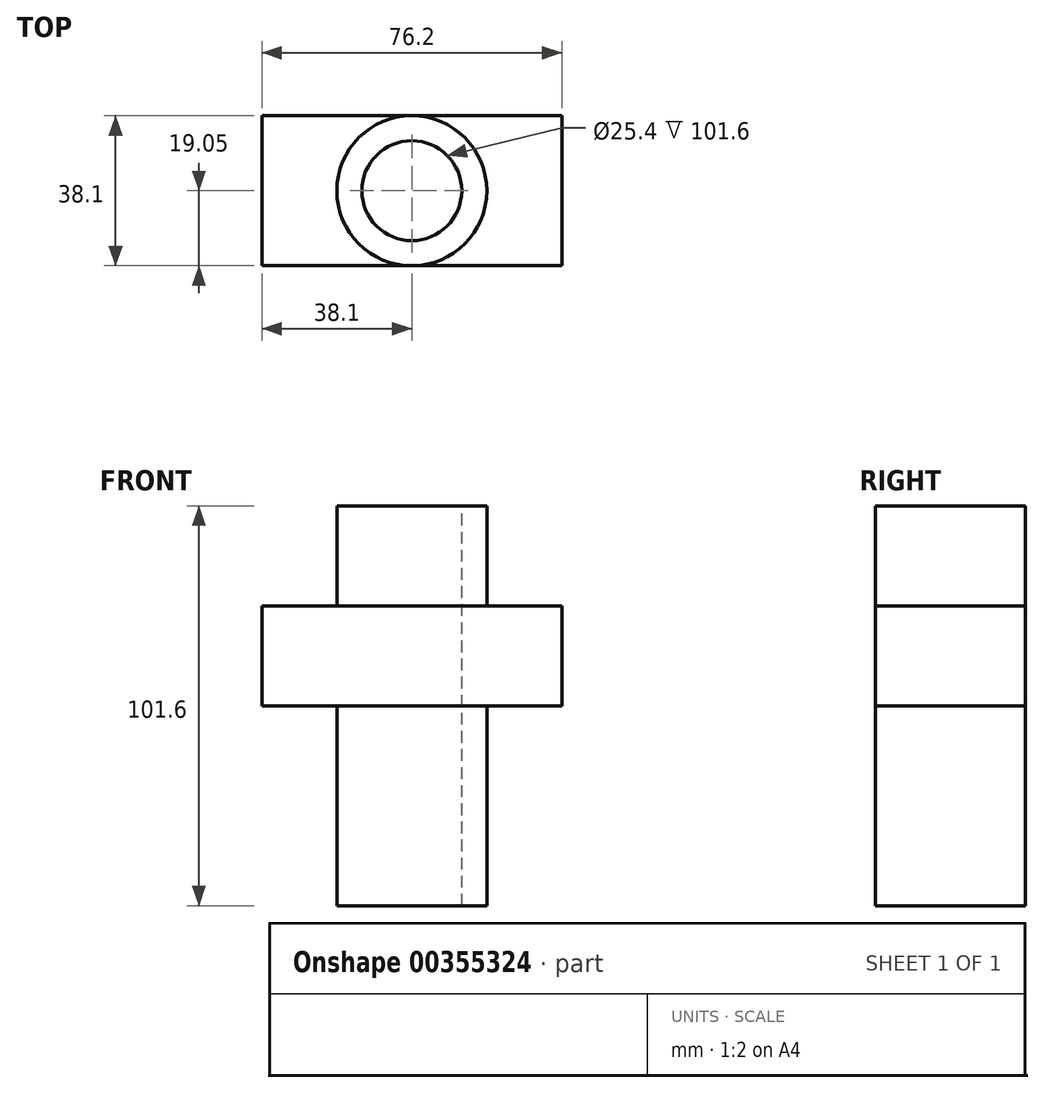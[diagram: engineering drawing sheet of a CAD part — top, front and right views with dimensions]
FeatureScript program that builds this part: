
annotation { "Feature Type Name" : "Feature", "Feature Type Description" : "" }
export const myFeature = defineFeature(function(context is Context, id is Id, definition is map)
    precondition{}
    {
        {
            var Q0;
            Q0=qCreatedBy(makeId("Top.planeOp"),FACE);
            var sketch = newSketch(context, id + "F0", { "sketchPlane" : qUnion([Q0])});
            skLineSegment(sketch, "E0", {"start": v(0, 0) * mm, "end": v(0, 38.1) * mm});
            skLineSegment(sketch, "E1", {"start": v(0, 38.1) * mm, "end": v(76.2, 38.1) * mm});
            skLineSegment(sketch, "E2", {"start": v(76.2, 38.1) * mm, "end": v(76.2, 0) * mm});
            skLineSegment(sketch, "E3", {"start": v(76.2, 0) * mm, "end": v(0, 0) * mm});
            skCircle(sketch, "E4", {"center": v(38.1, 19.05) * mm, "radius": 9.53 * mm});
            skPoint(sketch, "E4.centerSnap0", {"position": v(0, 19.05) * mm});
            skPoint(sketch, "E4.centerSnap1", {"position": v(38.1, 38.1) * mm});
            skCircle(sketch, "E5", {"center": v(38.1, 19.05) * mm, "radius": 19.05 * mm});
            skSolve(sketch);
        }
        {
            var Q0;
            {var subQ0=sQuery(id+"F0.wireOp",EDGE,"E0");Q0=makeQuery(id+"F0.imprint","IMPRINT",FACE,{"disambiguationData":[TD([[makeQuery(id+"F0.imprint","IMPRINT",EDGE,{"derivedFrom":subQ0}),-1.0]])]});}
            var Q1;
            {var subQ0=sQuery(id+"F0.wireOp",EDGE,"E2");Q1=makeQuery(id+"F0.imprint","IMPRINT",FACE,{"disambiguationData":[TD([[makeQuery(id+"F0.imprint","IMPRINT",EDGE,{"derivedFrom":subQ0}),-1.0]])]});}
            extrude(context, id + "F1", {"entities" : qUnion([Q0, Q1]), "depth" : 25.4 * mm});
        }
        {
            var Q0;
            Q0=makeQuery(id+"F0.imprint","IMPRINT",FACE,{"disambiguationData":[TD([[makeQuery(id+"F0.imprint","IMPRINT",EDGE,{"derivedFrom":sQuery(id+"F0.wireOp",EDGE,"E4")}),1.0]])]});
            var Q1;
            Q1=makeQuery(id+"F0.imprint","IMPRINT",FACE,{"disambiguationData":[TD([[makeQuery(id+"F0.imprint","IMPRINT",EDGE,{"derivedFrom":sQuery(id+"F0.wireOp",EDGE,"E4")}),-1.0]])]});
            extrude(context, id + "F2", {"entities" : qUnion([Q0, Q1]), "depth" : 50.8 * mm});
        }
        {
            var Q0;
            Q0=makeQuery(id+"F2.opExtrude","CAP_FACE",FACE,{"disambiguationData":[OSD([sQuery(id+"F0.wireOp",EDGE,"E5")])],"isStart":false});
            var sketch = newSketch(context, id + "F3", { "sketchPlane" : qUnion([Q0])});
            skCircle(sketch, "E6", {"center": v(38.1, 19.05) * mm, "radius": 12.7 * mm});
            skSolve(sketch);
        }
        {
            var Q0;
            Q0=makeQuery(id+"F3.imprint","IMPRINT",FACE,{"disambiguationData":[TD([[makeQuery(id+"F3.imprint","IMPRINT",EDGE,{"derivedFrom":sQuery(id+"F3.wireOp",EDGE,"E6")}),1.0]])]});
            extrude(context, id + "F4", {"entities" : qUnion([Q0]), "operationType" : NewBodyOperationType.REMOVE, "endBound" : BoundingType.THROUGH_ALL, "oppositeDirection" : true, "depth" : 25.4 * mm});
        }
        {
            var Q0;
            Q0=makeQuery(id+"F2.opExtrude","CAP_FACE",FACE,{"disambiguationData":[OSD([sQuery(id+"F0.wireOp",EDGE,"E5")])],"isStart":true});
            extrude(context, id + "F5", {"entities" : qUnion([Q0]), "operationType" : NewBodyOperationType.ADD, "depth" : 50.8 * mm});
        }
    });
